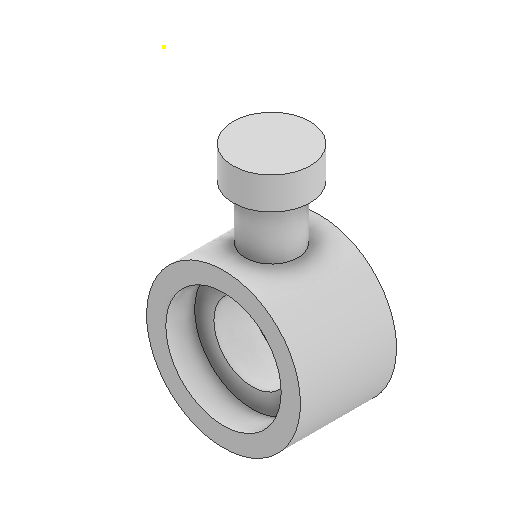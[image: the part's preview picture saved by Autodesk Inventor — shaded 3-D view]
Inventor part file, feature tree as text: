
AUTODESK INVENTOR PART (.ipt)
format: ipt  version: 2022 (Build 260153000, 153)  size: 140,800 bytes
history: native  units: mm
features: sketch x7, other x3
ambient origin geometry x8: Origin, YZ Plane, XZ Plane, XY Plane, X Axis, Y Axis, Z Axis, Center Point
bodies: Solid1 (feature_tree)
feature tree (10):
  other  "Sholder.ipt"
  other  "Solid1::Sholder.ipt"
  other  "TaggingFeature1"
  sketch  "Sketch1"  dims[d0=10.0mm]
  sketch  "Sketch2"
  sketch  "Sketch3"
  sketch  "Sketch4"
  sketch  "Sketch6"
  sketch  "Sketch7"
  sketch  "Sketch8"
